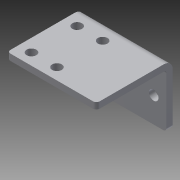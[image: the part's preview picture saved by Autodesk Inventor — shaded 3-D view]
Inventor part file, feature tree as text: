
AUTODESK INVENTOR PART (.ipt)
format: ipt  version: 2014 (Build 180170000, 170)  size: 170,496 bytes
history: native  units: in
note: dims shown in document units (in); Inventor stores cm internally (conversion verified against a paired STEP export)
features: sheet_metal_op x4, sketch x3, other x3, fillet x1, extrude x1
ambient origin geometry x8: Origin, YZ Plane, XZ Plane, XY Plane, X Axis, Y Axis, Z Axis, Center Point
bodies: Solid1 (feature_tree)
feature tree (12):
  sheet_metal_op  "Face1"
  sheet_metal_op  "Flange1"
  fillet  "Fillet1"  Radius=1.75in
  extrude  "Extrusion1"  Depth=0.19in
  sketch  "Sketch1"  dims[d1=1.0in d2=0.19in]
  other  "Plate1"
  sketch  "Sketch2"  dims[d4=0.7874in d6=1.0in d7=0.3937in d9=1.0in]
  other  "Plate2"
  sheet_metal_op  "Bend1"
  sheet_metal_op  "Corner1"
  sketch  "Sketch3"  dims[d11=0.125in d12=0.125in d13=0.0625in d14=0.25in d15=0.125in d16=1.5in d17=90.0deg d18=0.05in d19=0.5in d20=0.125in d21=0.125in d22=0.0625in d23=1.35in d24=0.75in d27=0.19in d28=0.125in d29=0.2265in d30=1.0in d31=0.0in d32=0.25in d33=0.875in]
  other  "Definition1"
